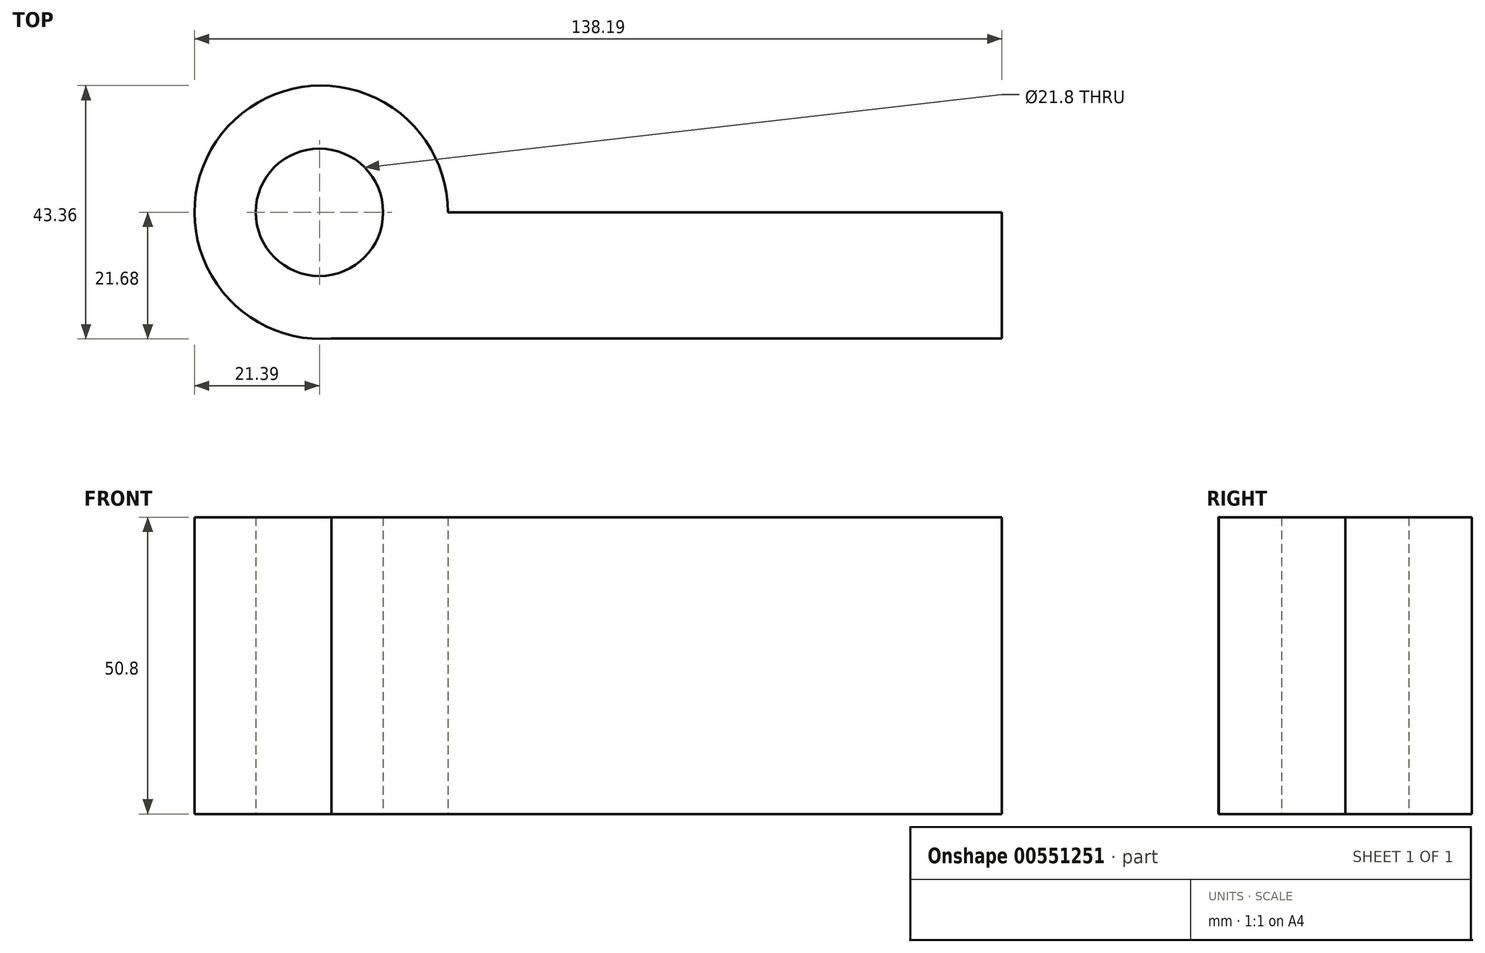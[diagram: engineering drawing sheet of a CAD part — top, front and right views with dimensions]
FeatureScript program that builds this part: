
annotation { "Feature Type Name" : "Feature", "Feature Type Description" : "" }
export const myFeature = defineFeature(function(context is Context, id is Id, definition is map)
    precondition{}
    {
        {
            var Q0;
            Q0=qCreatedBy(makeId("Top.planeOp"),FACE);
            var sketch = newSketch(context, id + "F0", { "sketchPlane" : qUnion([Q0])});
            skCircle(sketch, "E0", {"center": v(0, 0) * mm, "radius": 10.9 * mm});
            skCircle(sketch, "E1", {"center": v(0.3, 0) * mm, "radius": 21.68 * mm});
            skLineSegment(sketch, "E2.bottom", {"start": v(0.3, 0) * mm, "end": v(116.8, 0) * mm});
            skLineSegment(sketch, "E2.top", {"start": v(0.3, -21.6) * mm, "end": v(116.8, -21.6) * mm});
            skLineSegment(sketch, "E2.left", {"start": v(0.3, 0) * mm, "end": v(0.3, -21.6) * mm});
            skLineSegment(sketch, "E2.right", {"start": v(116.8, 0) * mm, "end": v(116.8, -21.6) * mm});
            skSolve(sketch);
        }
        {
            var Q0;
            {var subQ5=sQuery(id+"F0.wireOp",EDGE,"E2.bottom");var subQ7=sQuery(id+"F0.wireOp",EDGE,"E0");var subQ8=makeQuery(id+"F0.imprint","INTERSECT",VERTEX,{"derivedFrom":[subQ7,subQ5]});Q0=makeQuery(id+"F0.imprint","IMPRINT",FACE,{"disambiguationData":[TD([[makeQuery(id+"F0.imprint","IMPRINT",EDGE,{"disambiguationData":[TD([[subQ8,-1.0]])],"derivedFrom":subQ7}),-1.0]])]});}
            var Q1;
            {var subQ5=sQuery(id+"F0.wireOp",EDGE,"E2.bottom");var subQ7=sQuery(id+"F0.wireOp",EDGE,"E0");var subQ8=makeQuery(id+"F0.imprint","INTERSECT",VERTEX,{"derivedFrom":[subQ7,subQ5]});Q1=makeQuery(id+"F0.imprint","IMPRINT",FACE,{"disambiguationData":[TD([[makeQuery(id+"F0.imprint","IMPRINT",EDGE,{"disambiguationData":[TD([[subQ8,1.0]])],"derivedFrom":subQ7}),-1.0]])]});}
            var Q2;
            {var subQ5=sQuery(id+"F0.wireOp",EDGE,"E2.right");Q2=makeQuery(id+"F0.imprint","IMPRINT",FACE,{"disambiguationData":[TD([[makeQuery(id+"F0.imprint","IMPRINT",EDGE,{"derivedFrom":subQ5}),-1.0]])]});}
            extrude(context, id + "F1", {"entities" : qUnion([Q0, Q1, Q2]), "endBound" : BoundingType.SYMMETRIC, "depth" : 50.8 * mm, "offsetDistance" : 25.4 * mm});
        }
    });
